# Revit family: S 1062 LOT
name_source: partatom
category: Lighting Fixtures
revit_build: Autodesk Revit 2017 (Build: 20160225_1515(x64)
units: mm (PartAtom-declared; Revit-internal decimal feet)

## family parameters
Cut with Voids When Loaded = No
Host = Face
Light Source = Yes
Part Type = Normal
Room Calculation Point = No
Round Connector Dimension = Use Diameter
Shared = No

## types (2) — shared parameters
Apparent Load = 72 VA
Color Filter = 16777215
Default Elevation = 1219 mm
Dimming Lamp Color Temperature Shift = <None>
Emit Shape Visible in Rendering = Yes
Emit from Circle Diameter = 595 mm  [stored 1.9521 ft]
Manufacturer = ARLIGHT
Model = S 1062 LOT
Tilt Angle = 90.00°
Type Comments = Pendant Lotus
Type Image = <None>
Wattage Comments = 72W

## per-type parameters (varying)
| type | Photometric Web File |
| SLOT.620.72.30 | s-1062-lot-72w-3k-80ra-sa-07.ies |
| SLOT.620.72.40 | s-1062-lot-72w-4k-80ra-sa-07.ies |

note: [stored X ft] marks values corroborated as IEEE doubles in the binary element streams (Revit-internal decimal feet)

## geometry (parser evidence)
native form markers: Sweep x3
no freeform markers — native parametric forms only
